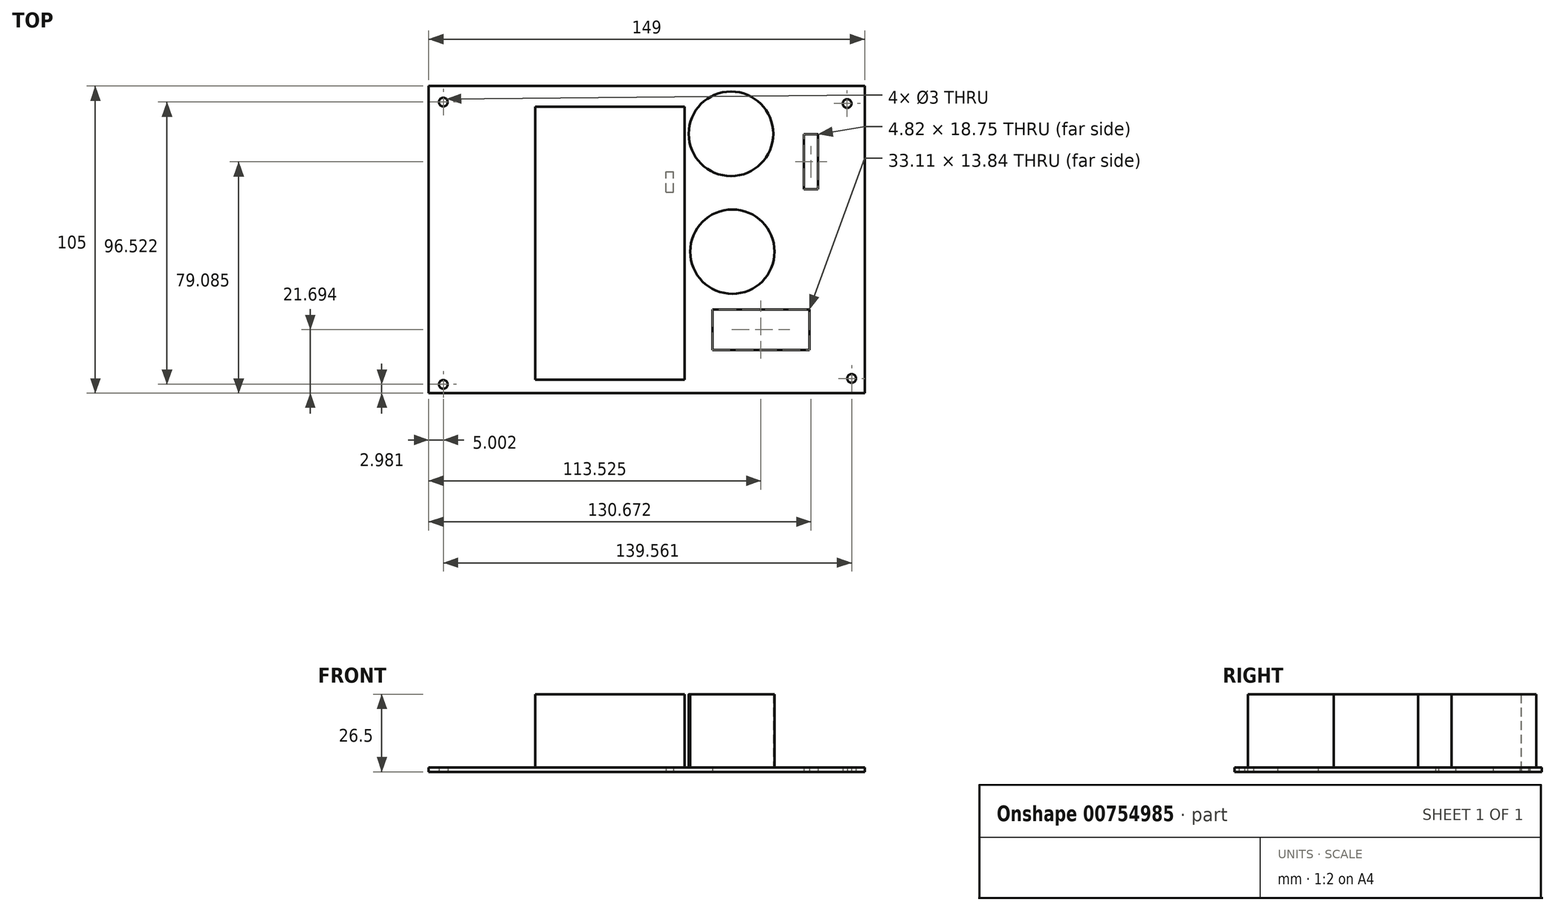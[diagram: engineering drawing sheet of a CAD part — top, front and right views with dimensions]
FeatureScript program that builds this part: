
annotation { "Feature Type Name" : "Feature", "Feature Type Description" : "" }
export const myFeature = defineFeature(function(context is Context, id is Id, definition is map)
    precondition{}
    {
        {
            var Q0;
            Q0=qCreatedBy(makeId("Top.planeOp"),FACE);
            var sketch = newSketch(context, id + "F0", { "sketchPlane" : qUnion([Q0])});
            skLineSegment(sketch, "E0.bottom", {"start": v(10.8, 118.57) * mm, "end": v(159.8, 118.57) * mm});
            skLineSegment(sketch, "E0.top", {"start": v(10.8, 13.57) * mm, "end": v(159.8, 13.57) * mm});
            skLineSegment(sketch, "E0.left", {"start": v(10.8, 118.57) * mm, "end": v(10.8, 13.57) * mm});
            skLineSegment(sketch, "E0.right", {"start": v(159.8, 118.57) * mm, "end": v(159.8, 13.57) * mm});
            skCircle(sketch, "E1", {"center": v(15.8, 113.07) * mm, "radius": 1.5 * mm});
            skCircle(sketch, "E2", {"center": v(15.8, 16.55) * mm, "radius": 1.5 * mm});
            skCircle(sketch, "E3", {"center": v(153.8, 112.57) * mm, "radius": 1.5 * mm});
            skCircle(sketch, "E4", {"center": v(155.36, 18.57) * mm, "radius": 1.5 * mm});
            skLineSegment(sketch, "E5.bottom", {"start": v(139.06, 83.28) * mm, "end": v(143.88, 83.28) * mm});
            skLineSegment(sketch, "E5.top", {"start": v(139.06, 102.03) * mm, "end": v(143.88, 102.03) * mm});
            skLineSegment(sketch, "E5.left", {"start": v(139.06, 83.28) * mm, "end": v(139.06, 102.03) * mm});
            skLineSegment(sketch, "E5.right", {"start": v(143.88, 83.28) * mm, "end": v(143.88, 102.03) * mm});
            skLineSegment(sketch, "E6.bottom", {"start": v(91.88, 82.3) * mm, "end": v(94.39, 82.3) * mm});
            skLineSegment(sketch, "E6.top", {"start": v(91.88, 89.2) * mm, "end": v(94.39, 89.2) * mm});
            skLineSegment(sketch, "E6.left", {"start": v(91.88, 82.3) * mm, "end": v(91.88, 89.2) * mm});
            skLineSegment(sketch, "E6.right", {"start": v(94.39, 82.3) * mm, "end": v(94.39, 89.2) * mm});
            skLineSegment(sketch, "E7.bottom", {"start": v(107.77, 28.34) * mm, "end": v(140.88, 28.34) * mm});
            skLineSegment(sketch, "E7.top", {"start": v(107.77, 42.18) * mm, "end": v(140.88, 42.18) * mm});
            skLineSegment(sketch, "E7.left", {"start": v(107.77, 28.34) * mm, "end": v(107.77, 42.18) * mm});
            skLineSegment(sketch, "E7.right", {"start": v(140.88, 28.34) * mm, "end": v(140.88, 42.18) * mm});
            skLineSegment(sketch, "E8", {"start": v(143.49, 108.82) * mm, "end": v(130.15, 85.3) * mm});
            skSolve(sketch);
        }
        {
            var Q0;
            Q0 = qSketchRegion(id + "F0", true);
            extrude(context, id + "F1", {"entities" : qUnion([Q0]), "depth" : 1.5 * mm, "offsetDistance" : 25 * mm});
        }
        {
            var Q0;
            Q0=makeQuery(id+"F1.opExtrude","CAP_FACE",FACE,{"disambiguationData":[OSD([sQuery(id+"F0.wireOp",EDGE,"E0.bottom"),sQuery(id+"F0.wireOp",EDGE,"E0.top"),sQuery(id+"F0.wireOp",EDGE,"E0.left"),sQuery(id+"F0.wireOp",EDGE,"E0.right"),sQuery(id+"F0.wireOp",EDGE,"E1"),sQuery(id+"F0.wireOp",EDGE,"E2"),sQuery(id+"F0.wireOp",EDGE,"E3"),sQuery(id+"F0.wireOp",EDGE,"E4")])],"isStart":false});
            var sketch = newSketch(context, id + "F2", { "sketchPlane" : qUnion([Q0])});
            skCircle(sketch, "E9", {"center": v(114.11, 102.22) * mm, "radius": 14.45 * mm});
            skCircle(sketch, "E10", {"center": v(114.58, 61.91) * mm, "radius": 14.42 * mm});
            skLineSegment(sketch, "E11.bottom", {"start": v(47.25, 111.54) * mm, "end": v(98.3, 111.54) * mm});
            skLineSegment(sketch, "E11.top", {"start": v(47.25, 18.13) * mm, "end": v(98.3, 18.13) * mm});
            skLineSegment(sketch, "E11.left", {"start": v(47.25, 111.54) * mm, "end": v(47.25, 18.13) * mm});
            skLineSegment(sketch, "E11.right", {"start": v(98.3, 111.54) * mm, "end": v(98.3, 18.13) * mm});
            skSolve(sketch);
        }
        {
            var Q0;
            Q0 = qSketchRegion(id + "F2", true);
            extrude(context, id + "F3", {"entities" : qUnion([Q0]), "operationType" : NewBodyOperationType.ADD, "depth" : 25 * mm, "offsetDistance" : 25 * mm});
        }
    });
